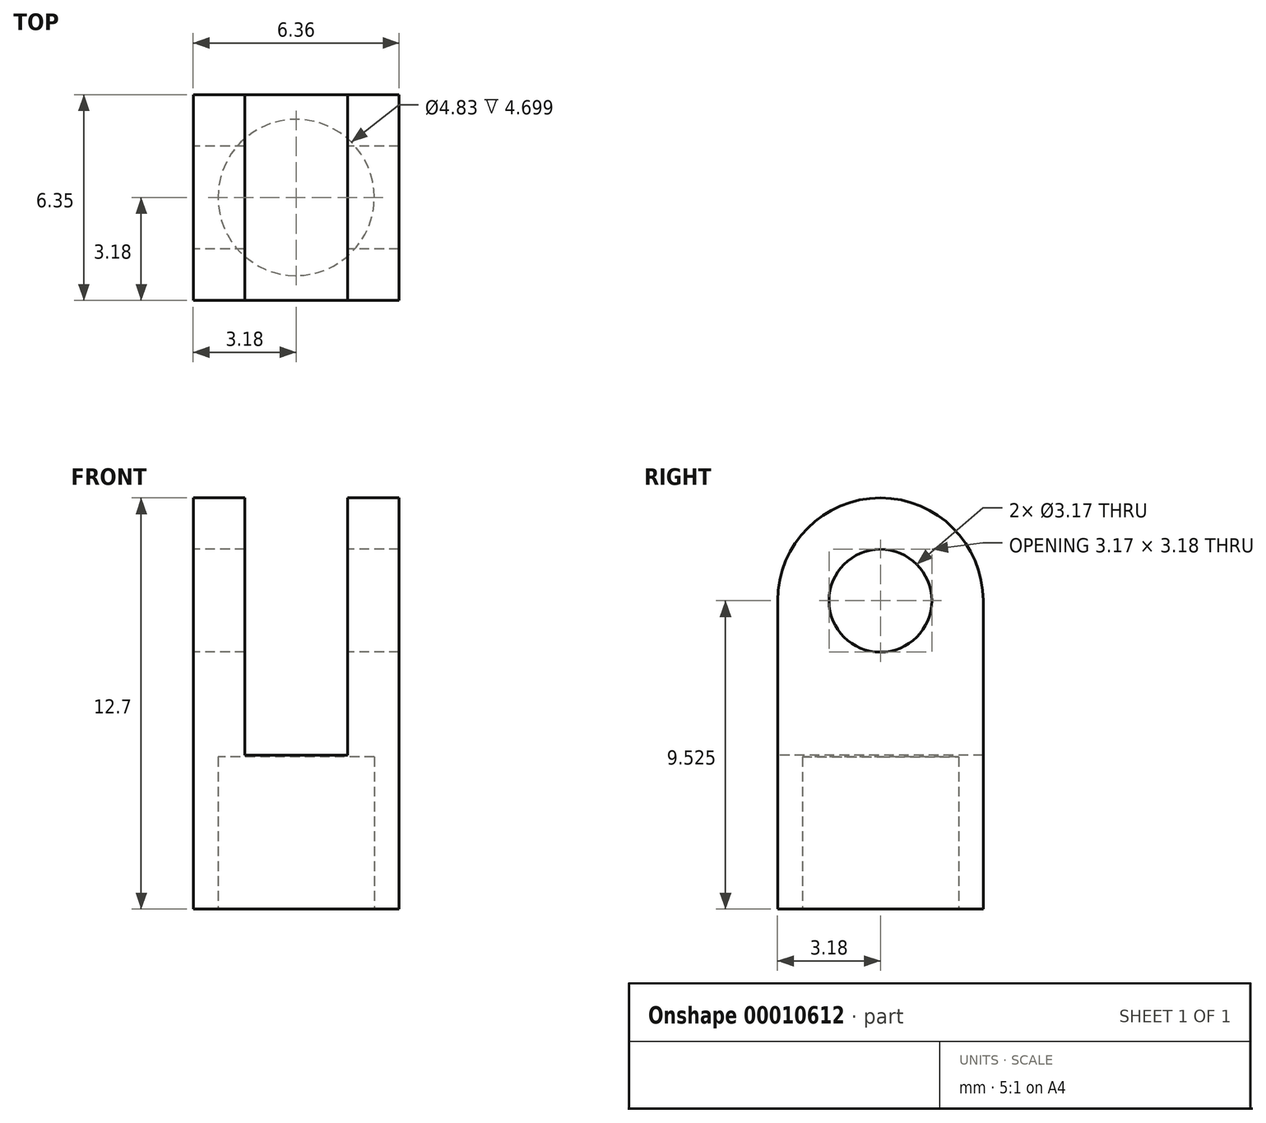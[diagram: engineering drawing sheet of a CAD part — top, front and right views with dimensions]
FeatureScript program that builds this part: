
annotation { "Feature Type Name" : "Feature", "Feature Type Description" : "" }
export const myFeature = defineFeature(function(context is Context, id is Id, definition is map)
    precondition{}
    {
        {
            var Q0;
            Q0=qCreatedBy(makeId("Top.planeOp"),FACE);
            var sketch = newSketch(context, id + "F0", { "sketchPlane" : qUnion([Q0])});
            skLineSegment(sketch, "E0.rect.bottom", {"start": v(3.18, -3.17) * mm, "end": v(-3.17, -3.18) * mm});
            skLineSegment(sketch, "E0.rect.top", {"start": v(3.17, 3.18) * mm, "end": v(-3.18, 3.17) * mm});
            skLineSegment(sketch, "E0.rect.left", {"start": v(3.18, -3.17) * mm, "end": v(3.17, 3.18) * mm});
            skLineSegment(sketch, "E0.rect.right", {"start": v(-3.17, -3.18) * mm, "end": v(-3.18, 3.17) * mm});
            skPoint(sketch, "E0.rect.middle", {"position": v(0, 0) * mm});
            skCircle(sketch, "E1", {"center": v(0, 0) * mm, "radius": 2.41 * mm});
            skSolve(sketch);
        }
        {
            var Q0;
            Q0=qSketchRegion(id+"F0",true);
            var Q1;
            Q1=makeQuery(id+"F0.imprint","IMPRINT",FACE,{"disambiguationData":[TD([[makeQuery(id+"F0.imprint","IMPRINT",EDGE,{"derivedFrom":sQuery(id+"F0.wireOp",EDGE,"E1")}),1.0]])]});
            extrude(context, id + "F1", {"entities" : qUnion([Q0, Q1]), "depth" : 12.7 * mm});
        }
        {
            var Q0;
            Q0=makeQuery(id+"F0.imprint","IMPRINT",FACE,{"disambiguationData":[TD([[makeQuery(id+"F0.imprint","IMPRINT",EDGE,{"derivedFrom":sQuery(id+"F0.wireOp",EDGE,"E1")}),1.0]])]});
            extrude(context, id + "F2", {"entities" : qUnion([Q0]), "operationType" : NewBodyOperationType.REMOVE, "depth" : 4.7 * mm});
        }
        {
            var Q0;
            Q0=makeQuery(id+"F1.opExtrude","CAP_EDGE",EDGE,{"disambiguationData":[OSD([sQuery(id+"F0.wireOp",EDGE,"E0.rect.bottom")])],"isStart":false});
            var Q1;
            Q1=makeQuery(id+"F1.opExtrude","CAP_EDGE",EDGE,{"disambiguationData":[OSD([sQuery(id+"F0.wireOp",EDGE,"E0.rect.top")])],"isStart":false});
            fillet(context, id + "F3", {"entities" : qUnion([Q0, Q1]), "radius" : 3.17 * mm, "tangentPropagation" : true, "allowEdgeOverflow" : false});
        }
        {
            var Q0;
            Q0=makeQuery(id+"F1.opExtrude","SWEPT_FACE",FACE,{"disambiguationData":[OSD([sQuery(id+"F0.wireOp",EDGE,"E0.rect.right")])]});
            var sketch = newSketch(context, id + "F4", { "sketchPlane" : qUnion([Q0])});
            skCircle(sketch, "E2", {"center": v(0, 9.53) * mm, "radius": 1.59 * mm});
            skSolve(sketch);
        }
        {
            var Q0;
            Q0=qSketchRegion(id+"F4",true);
            extrude(context, id + "F5", {"entities" : qUnion([Q0]), "operationType" : NewBodyOperationType.REMOVE, "endBound" : BoundingType.UP_TO_NEXT, "oppositeDirection" : true, "depth" : 25.4 * mm});
        }
        {
            var Q0;
            Q0=makeQuery(id+"F1.opExtrude","SWEPT_FACE",FACE,{"disambiguationData":[OSD([sQuery(id+"F0.wireOp",EDGE,"E0.rect.bottom")])]});
            var sketch = newSketch(context, id + "F6", { "sketchPlane" : qUnion([Q0])});
            skLineSegment(sketch, "E3.bottom", {"start": v(-1.59, 4.75) * mm, "end": v(1.59, 4.75) * mm});
            skLineSegment(sketch, "E3.top", {"start": v(-1.59, 14.03) * mm, "end": v(1.59, 14.03) * mm});
            skLineSegment(sketch, "E3.left", {"start": v(-1.59, 4.75) * mm, "end": v(-1.59, 14.03) * mm});
            skLineSegment(sketch, "E3.right", {"start": v(1.59, 4.75) * mm, "end": v(1.59, 14.03) * mm});
            skSolve(sketch);
        }
        {
            var Q0;
            Q0=qSketchRegion(id+"F6",true);
            extrude(context, id + "F7", {"entities" : qUnion([Q0]), "operationType" : NewBodyOperationType.REMOVE, "endBound" : BoundingType.UP_TO_NEXT, "oppositeDirection" : true, "depth" : 25.4 * mm});
        }
    });
